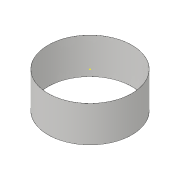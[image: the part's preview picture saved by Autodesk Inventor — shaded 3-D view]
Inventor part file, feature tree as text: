
AUTODESK INVENTOR PART (.ipt)
format: ipt  version: 2019 (Build 230136000, 136)  size: 83,456 bytes
history: native  units: in
note: dims shown in document units (in); Inventor stores cm internally (conversion verified against a paired STEP export)
features: sketch x3, extrude x2
ambient origin geometry x8: Origin, YZ Plane, XZ Plane, XY Plane, X Axis, Y Axis, Z Axis, Center Point
bodies: Solid1 (feature_tree)
feature tree (5):
  extrude  "Extrusion1"  Depth=0.5906in TaperAngle=0.0deg
  extrude  "Extrusion2"  [1 undecoded]
  sketch  "Sketch3"
  sketch  "Sketch1"  dims[d0=1.378in d1=0.5906in d2=0.0in]
  sketch  "Sketch2"  dims[d3=0.5906in d4=0.0in]
note: 1 required parameter value undecoded (feature->parameter linkage not recoverable at this tier; creation-order binding heuristic only, values carry confidence <= 0.55)
